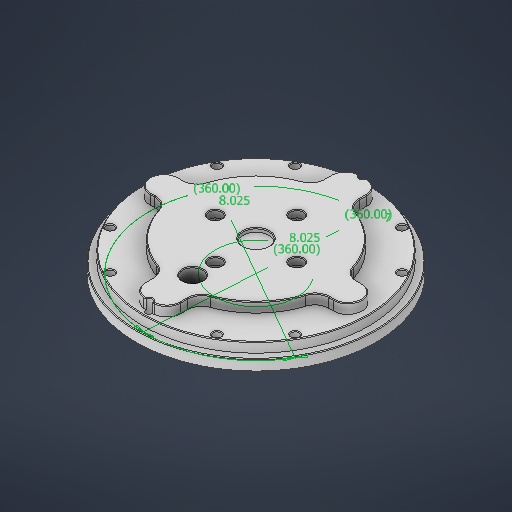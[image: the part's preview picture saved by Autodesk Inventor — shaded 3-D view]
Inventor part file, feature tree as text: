
AUTODESK INVENTOR PART (.ipt)
format: ipt  version: 2025 (Build 290162000, 162)  size: 606,720 bytes
history: native  units: in
note: dims shown in document units (in); Inventor stores cm internally (conversion verified against a paired STEP export)
features: sketch x17, extrude x11, hole x4, chamfer x4
ambient origin geometry x8: Origin, YZ Plane, XZ Plane, XY Plane, X Axis, Y Axis, Z Axis, Center Point
bodies: Solid1 (feature_tree)
feature tree (36):
  sketch  "Sketch1"  dims[d3=4.3307in d24=6.6929in]
  extrude  "Extrusion1"  Depth=6.6929in
  extrude  "Extrusion2"  Depth=5.9843in
  extrude  "Extrusion3"  Depth=0.9843in
  sketch  "Sketch2"  dims[d27=0.9843in d28=4.3307in]
  extrude  "Extrusion4"  Depth=0.3937in
  hole  "Hole1"  [1 undecoded]
  hole  "Hole2"  [1 undecoded]
  sketch  "Sketch4"  dims[d38=0.2953in d39=0.0in d40=2.2835in]
  extrude  "Extrusion5"  Depth=2.2835in
  extrude  "Extrusion6"  Depth=0.3543in
  hole  "Hole3"  [1 undecoded]
  chamfer  "Chamfer1"  Distance=0.7874in Angle=360.0deg
  chamfer  "Chamfer2"  Distance=0.0591in
  hole  "Hole5"  [1 undecoded]
  extrude  "Extrusion9"  Depth=0.1673in TaperAngle=360.0deg
  chamfer  "Chamfer3"  Distance=0.0197in Angle=45.0deg
  extrude  "Extrusion10"  Depth=0.1673in TaperAngle=45.0deg
  chamfer  "Chamfer4"  Distance=3.7402in
  sketch  "Sketch11"  dims[d74=0.4724in d75=0.0in d76=0.1969in d77=4.7244in d79=360.0deg d81=0.2165in d82=0.3937in d83=0.1575in d84=0.0787in d85=90.0deg d86=0.3937in d87=0.8108in d88=0.0197in d89=0.0787in d90=45.0deg d91=0.0197in d92=0.0787in d93=45.0deg d107=3.7402in d108=0.1969in d109=6.2992in d111=360.0deg d113=0.1969in d114=0.7874in d115=0.748in d116=0.3543in d117=90.0deg d118=0.7874in d119=0.8108in d139=0.7185in d140=3.1496in d141=0.7185in d142=3.1496in d144=360.0deg d146=0.0984in d147=0.0in d148=0.0197in d149=0.0787in d150=45.0deg d151=0.5512in d152=1.7717in d153=0.0in d154=0.0in d155=0.0197in d156=0.0787in d157=45.0deg d158=0.5512in d159=1.7717in d160=0.3159in d161=4.7244in d163=360.0deg d165=0.2756in d166=0.7874in d168=360.0deg d170=0.3159in d171=1.5748in d173=360.0deg d175=0.1673in d176=0.0in d177=0.1575in d178=0.0in d179=0.1673in d180=0.0in d137=0.0197in d138=0.0344in]
  extrude  "Extrusion11"  Depth=0.1673in
  extrude  "Extrusion12"  Depth=0.1673in TaperAngle=360.0deg
  extrude  "Extrusion13"  Depth=0.1673in
  sketch  "Sketch Circular Pattern1"  dims[d25=6.2992in d26=5.9843in]
  sketch  "Sketch3"  dims[d31=0.3937in d32=0.3937in]
  sketch  "Sketch Circular Pattern2"  dims[d29=0.7874in d30=0.3937in]
  sketch  "Sketch5"  dims[d41=0.3543in d42=0.1969in]
  sketch  "Sketch Circular Pattern3"  dims[d34=0.8465in d35=0.0in d36=0.5709in d37=0.0in]
  sketch  "Sketch7"  dims[d56=5.9843in]
  sketch  "Sketch Circular Pattern5"  dims[d43=1.5748in d45=360.0deg d47=0.1969in d48=0.0in]
  sketch  "Sketch9"  dims[d69=3.1496in]
  sketch  "Sketch Circular Pattern6"  dims[d49=0.2165in d50=0.7874in d51=0.1575in d52=0.0787in d53=90.0deg d54=0.315in d55=0.8108in]
  sketch  "Sketch10"  dims[d71=0.7874in d72=0.0591in d73=0.0in]
  sketch  "Sketch Circular Pattern7"  dims[d57=0.1378in d58=0.7874in d60=360.0deg]
  sketch  "Sketch Circular Pattern8"  dims[d62=0.1772in d63=0.315in d64=0.1575in d65=0.0787in d66=90.0deg d67=0.4646in d68=0.8108in]
  sketch  "Sketch Circular Pattern9"  dims[d70=0.1969in]
note: 4 required parameter values undecoded (feature->parameter linkage not recoverable at this tier; creation-order binding heuristic only, values carry confidence <= 0.55)
